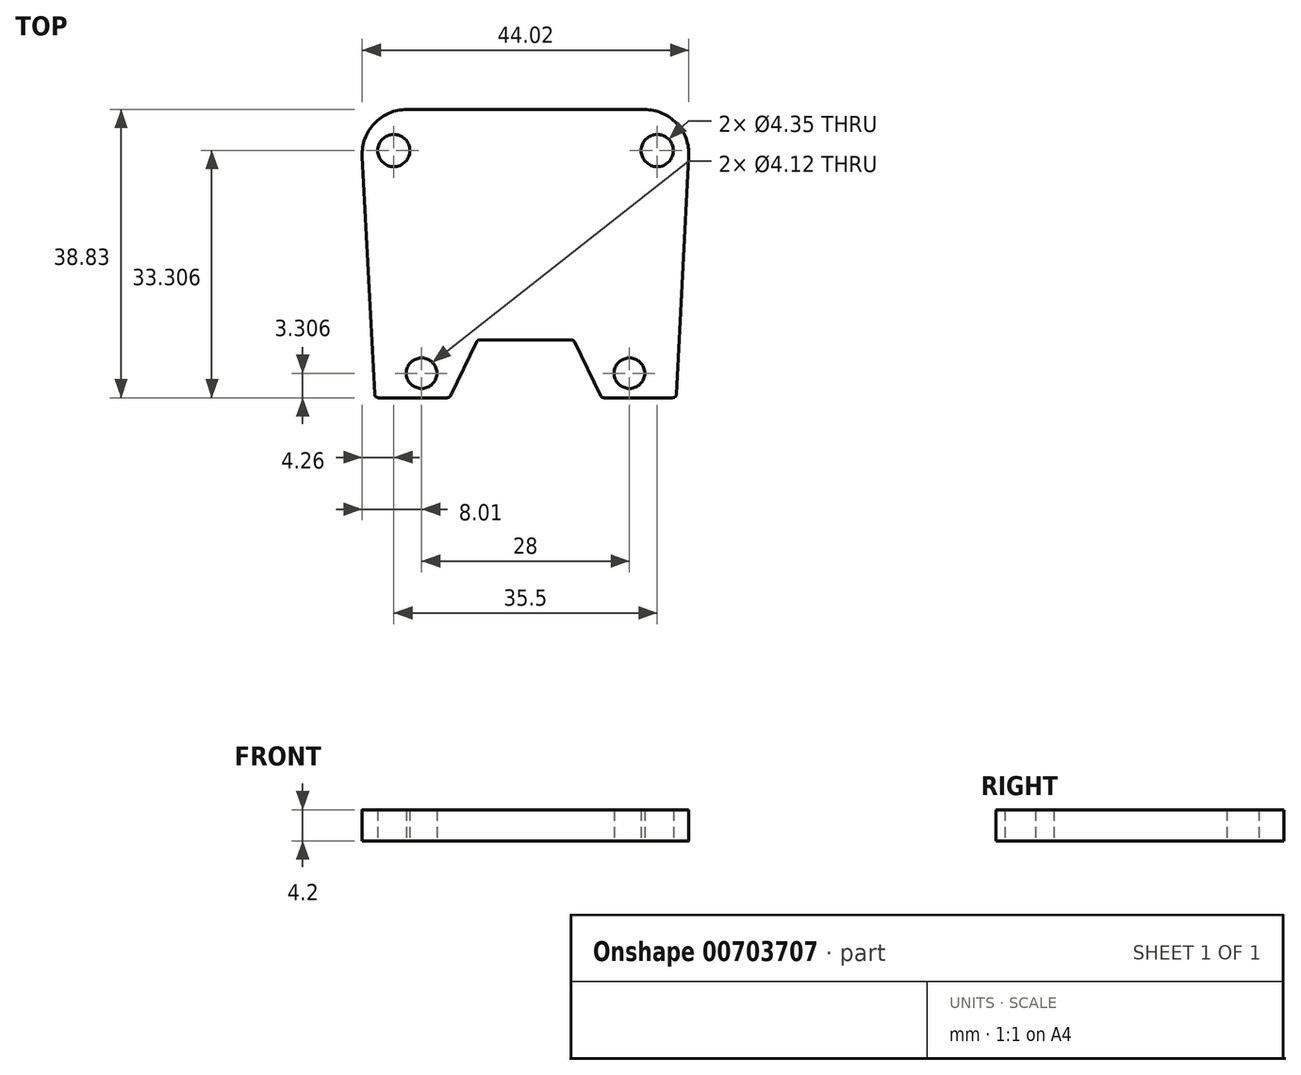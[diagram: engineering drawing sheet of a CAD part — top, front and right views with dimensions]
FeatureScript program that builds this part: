
annotation { "Feature Type Name" : "Feature", "Feature Type Description" : "" }
export const myFeature = defineFeature(function(context is Context, id is Id, definition is map)
    precondition{}
    {
        {
            var Q0;
            Q0=qCreatedBy(makeId("Top.planeOp"),FACE);
            var sketch = newSketch(context, id + "F0", { "sketchPlane" : qUnion([Q0])});
            skCircle(sketch, "E0", {"center": v(-17.75, 17.74) * mm, "radius": 2.17 * mm});
            skCircle(sketch, "E1", {"center": v(-14, -12.26) * mm, "radius": 2.06 * mm});
            skLineSegment(sketch, "E2", {"start": v(0, 23.26) * mm, "end": v(-16.01, 23.26) * mm});
            skLineSegment(sketch, "E3", {"start": v(-22, 16.94) * mm, "end": v(-20.34, -15.1) * mm});
            skLineSegment(sketch, "E4", {"start": v(-19.84, -15.57) * mm, "end": v(-10.55, -15.57) * mm});
            skLineSegment(sketch, "E5", {"start": v(-10.1, -15.28) * mm, "end": v(-6.6, -8.04) * mm});
            skLineSegment(sketch, "E6", {"start": v(-6.14, -7.76) * mm, "end": v(0, -7.76) * mm});
            skPoint(sketch, "E7.visualSharp", {"position": v(-22.33, 23.26) * mm});
            skArc(sketch, "E7.filletArc", {"start": v(-16.01, 23.26) * mm, "mid": v(-20.36, 21.39) * mm, "end": v(-22, 16.94) * mm});
            skPoint(sketch, "E8.visualSharp", {"position": v(-20.31, -15.57) * mm});
            skArc(sketch, "E8.filletArc", {"start": v(-20.34, -15.1) * mm, "mid": v(-20.18, -15.43) * mm, "end": v(-19.84, -15.57) * mm});
            skPoint(sketch, "E9.visualSharp", {"position": v(-10.23, -15.57) * mm});
            skArc(sketch, "E9.filletArc", {"start": v(-10.55, -15.57) * mm, "mid": v(-10.28, -15.49) * mm, "end": v(-10.1, -15.28) * mm});
            skPoint(sketch, "E10.visualSharp", {"position": v(-6.46, -7.76) * mm});
            skArc(sketch, "E10.filletArc", {"start": v(-6.14, -7.76) * mm, "mid": v(-6.4, -7.83) * mm, "end": v(-6.6, -8.04) * mm});
            skLineSegment(sketch, "E11.MirrorCS", {"start": v(0, 23.26) * mm, "end": v(16.01, 23.26) * mm});
            skArc(sketch, "E12.MirrorCS", {"start": v(16.01, 23.26) * mm, "mid": v(20.36, 21.39) * mm, "end": v(22, 16.94) * mm});
            skCircle(sketch, "E13.MirrorC", {"center": v(17.75, 17.74) * mm, "radius": 2.17 * mm});
            skLineSegment(sketch, "E14.MirrorCS", {"start": v(22, 16.94) * mm, "end": v(20.34, -15.1) * mm});
            skLineSegment(sketch, "E15.MirrorCS", {"start": v(19.84, -15.57) * mm, "end": v(10.55, -15.57) * mm});
            skLineSegment(sketch, "E16.MirrorCS", {"start": v(10.1, -15.28) * mm, "end": v(6.6, -8.04) * mm});
            skLineSegment(sketch, "E17.MirrorCS", {"start": v(6.14, -7.76) * mm, "end": v(0, -7.76) * mm});
            skArc(sketch, "E18.MirrorCS", {"start": v(6.14, -7.76) * mm, "mid": v(6.4, -7.83) * mm, "end": v(6.6, -8.04) * mm});
            skArc(sketch, "E19.MirrorCS", {"start": v(10.55, -15.57) * mm, "mid": v(10.28, -15.49) * mm, "end": v(10.1, -15.28) * mm});
            skArc(sketch, "E20.MirrorCS", {"start": v(20.34, -15.1) * mm, "mid": v(20.18, -15.43) * mm, "end": v(19.84, -15.57) * mm});
            skCircle(sketch, "E21.MirrorC", {"center": v(14, -12.26) * mm, "radius": 2.06 * mm});
            skSolve(sketch);
        }
        {
            var Q0;
            Q0 = qSketchRegion(id + "F0", true);
            extrude(context, id + "F1", {"entities" : qUnion([Q0]), "depth" : 4.2 * mm, "offsetDistance" : 25 * mm});
        }
    });
